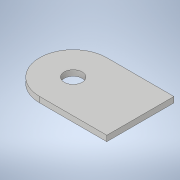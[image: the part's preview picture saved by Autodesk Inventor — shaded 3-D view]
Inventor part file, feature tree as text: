
AUTODESK INVENTOR PART (.ipt)
format: ipt  version: 2021 (Build 250183000, 183)  size: 104,960 bytes
history: native  units: in
note: dims shown in document units (in); Inventor stores cm internally (conversion verified against a paired STEP export)
features: extrude x2, sketch x2
ambient origin geometry x8: Origin, YZ Plane, XZ Plane, XY Plane, X Axis, Y Axis, Z Axis, Center Point
bodies: Solid1 (feature_tree)
feature tree (4):
  extrude  "Extrusion1"  Depth=0.75in
  extrude  "Extrusion2"  Depth=0.75in
  sketch  "Sketch1"  dims[d0=0.201in d1=0.75in]
  sketch  "Sketch2"  dims[d2=0.75in d3=0.75in d4=0.0625in d5=0.0in d7=1.0in d8=2.0in d9=0.0in d10=0.5in d11=0.0344in d12=0.5in d13=0.0344in]
